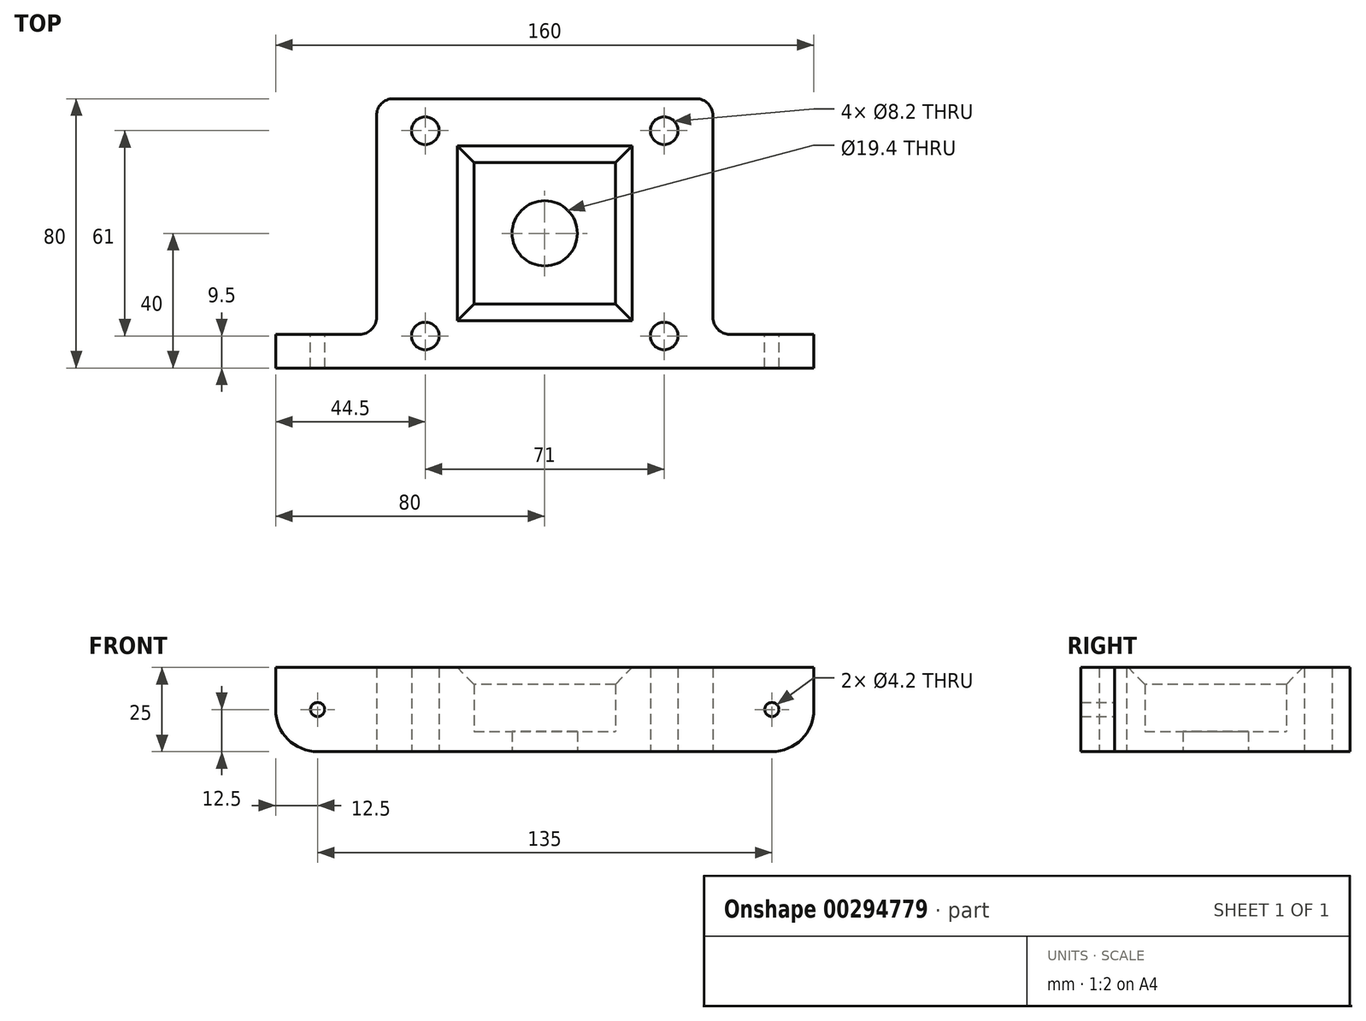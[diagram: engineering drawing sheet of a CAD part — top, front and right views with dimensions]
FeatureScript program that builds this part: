
annotation { "Feature Type Name" : "Feature", "Feature Type Description" : "" }
export const myFeature = defineFeature(function(context is Context, id is Id, definition is map)
    precondition{}
    {
        {
            var Q0;
            Q0=qCreatedBy(makeId("Top.planeOp"),FACE);
            var sketch = newSketch(context, id + "F0", { "sketchPlane" : qUnion([Q0])});
            skLineSegment(sketch, "E0.top", {"start": v(-50, -40) * mm, "end": v(50, -40) * mm});
            skPoint(sketch, "E0.middle", {"position": v(0, 0) * mm});
            skPoint(sketch, "E1.orphan", {"position": v(-50, 40) * mm});
            skPoint(sketch, "E2.orphan", {"position": v(50, 40) * mm});
            skPoint(sketch, "E0.left.start.orphan", {"position": v(-50, 21) * mm});
            skPoint(sketch, "E0.right.start.orphan", {"position": v(50, 21) * mm});
            skLineSegment(sketch, "E3", {"start": v(-50, 40) * mm, "end": v(-50, -40) * mm});
            skLineSegment(sketch, "E4", {"start": v(50, 40) * mm, "end": v(50, -40) * mm});
            skLineSegment(sketch, "E5", {"start": v(50, 40) * mm, "end": v(-50, 40) * mm});
            skLineSegment(sketch, "E6", {"start": v(50, 21) * mm, "end": v(21, 21) * mm, "construction": true});
            skLineSegment(sketch, "E7", {"start": v(-50, -40) * mm, "end": v(-21, -21) * mm, "construction": true});
            skLineSegment(sketch, "E8", {"start": v(-21, -21) * mm, "end": v(-50, -21) * mm, "construction": true});
            skLineSegment(sketch, "E9", {"start": v(-21, -21) * mm, "end": v(-21, -40) * mm, "construction": true});
            skLineSegment(sketch, "E10", {"start": v(-21, -40) * mm, "end": v(-50, -21) * mm, "construction": true});
            skLineSegment(sketch, "E11", {"start": v(-50, 21) * mm, "end": v(-21, 21) * mm, "construction": true});
            skLineSegment(sketch, "E12", {"start": v(21, -21) * mm, "end": v(21, -40) * mm, "construction": true});
            skLineSegment(sketch, "E13", {"start": v(21, -21) * mm, "end": v(50, -21) * mm, "construction": true});
            skLineSegment(sketch, "E14", {"start": v(50, -21) * mm, "end": v(21, -40) * mm, "construction": true});
            skLineSegment(sketch, "E15", {"start": v(50, -40) * mm, "end": v(21, -21) * mm, "construction": true});
            skCircle(sketch, "E16", {"center": v(-35.5, -30.5) * mm, "radius": 4.1 * mm});
            skCircle(sketch, "E17", {"center": v(35.5, -30.5) * mm, "radius": 4.1 * mm});
            skLineSegment(sketch, "E18", {"start": v(-21, 21) * mm, "end": v(-21, 40) * mm, "construction": true});
            skLineSegment(sketch, "E19", {"start": v(21, 21) * mm, "end": v(21, 40) * mm, "construction": true});
            skLineSegment(sketch, "E20", {"start": v(-21, 40) * mm, "end": v(-50, 21) * mm, "construction": true});
            skLineSegment(sketch, "E21", {"start": v(-50, 40) * mm, "end": v(-21, 21) * mm, "construction": true});
            skLineSegment(sketch, "E22", {"start": v(21, 40) * mm, "end": v(50, 21) * mm, "construction": true});
            skLineSegment(sketch, "E23", {"start": v(50, 40) * mm, "end": v(21, 21) * mm, "construction": true});
            skCircle(sketch, "E24", {"center": v(-35.5, 30.5) * mm, "radius": 4.1 * mm});
            skCircle(sketch, "E25", {"center": v(35.5, 30.5) * mm, "radius": 4.1 * mm});
            skCircle(sketch, "E26", {"center": v(0, 0) * mm, "radius": 9.7 * mm});
            skLineSegment(sketch, "E27.bottom", {"start": v(50, -40) * mm, "end": v(80, -40) * mm});
            skLineSegment(sketch, "E27.top", {"start": v(50, -30) * mm, "end": v(80, -30) * mm});
            skLineSegment(sketch, "E27.left", {"start": v(50, -40) * mm, "end": v(50, -30) * mm});
            skLineSegment(sketch, "E27.right", {"start": v(80, -40) * mm, "end": v(80, -30) * mm});
            skLineSegment(sketch, "E28.bottom", {"start": v(-50, -40) * mm, "end": v(-80, -40) * mm});
            skLineSegment(sketch, "E28.top", {"start": v(-50, -30) * mm, "end": v(-80, -30) * mm});
            skLineSegment(sketch, "E28.left", {"start": v(-50, -40) * mm, "end": v(-50, -30) * mm});
            skLineSegment(sketch, "E28.right", {"start": v(-80, -40) * mm, "end": v(-80, -30) * mm});
            skLineSegment(sketch, "E29", {"start": v(-21, 21) * mm, "end": v(21, 21) * mm});
            skLineSegment(sketch, "E30", {"start": v(21, 21) * mm, "end": v(21, -21) * mm});
            skLineSegment(sketch, "E31", {"start": v(21, -21) * mm, "end": v(-21, -21) * mm});
            skLineSegment(sketch, "E32", {"start": v(-21, -21) * mm, "end": v(-21, 21) * mm});
            skSolve(sketch);
        }
        {
            var Q0;
            Q0=makeQuery(id+"F0.imprint","IMPRINT",FACE,{"disambiguationData":[TD([[makeQuery(id+"F0.imprint","IMPRINT",EDGE,{"derivedFrom":sQuery(id+"F0.wireOp",EDGE,"E0.top")}),1.0]])]});
            var Q1;
            Q1=makeQuery(id+"F0.imprint","IMPRINT",FACE,{"disambiguationData":[TD([[makeQuery(id+"F0.imprint","IMPRINT",EDGE,{"derivedFrom":sQuery(id+"F0.wireOp",EDGE,"E28.bottom")}),-1.0]])]});
            var Q2;
            Q2=makeQuery(id+"F0.imprint","IMPRINT",FACE,{"disambiguationData":[TD([[makeQuery(id+"F0.imprint","IMPRINT",EDGE,{"derivedFrom":sQuery(id+"F0.wireOp",EDGE,"E27.bottom")}),1.0]])]});
            extrude(context, id + "F1", {"entities" : qUnion([Q0, Q1, Q2]), "depth" : 25 * mm});
        }
        {
            var Q0;
            Q0=makeQuery(id+"F0.imprint","IMPRINT",FACE,{"disambiguationData":[TD([[makeQuery(id+"F0.imprint","IMPRINT",EDGE,{"derivedFrom":sQuery(id+"F0.wireOp",EDGE,"E26")}),-1.0]])]});
            extrude(context, id + "F2", {"entities" : qUnion([Q0]), "operationType" : NewBodyOperationType.ADD, "depth" : 6 * mm});
        }
        {
            var Q0;
            Q0=makeQuery(id+"F1.opExtrude","CAP_EDGE",EDGE,{"disambiguationData":[OSD([sQuery(id+"F0.wireOp",EDGE,"E29")])],"isStart":false});
            var Q1;
            Q1=makeQuery(id+"F1.opExtrude","CAP_EDGE",EDGE,{"disambiguationData":[OSD([sQuery(id+"F0.wireOp",EDGE,"E32")])],"isStart":false});
            var Q2;
            Q2=makeQuery(id+"F1.opExtrude","CAP_EDGE",EDGE,{"disambiguationData":[OSD([sQuery(id+"F0.wireOp",EDGE,"E31")])],"isStart":false});
            var Q3;
            Q3=makeQuery(id+"F1.opExtrude","CAP_EDGE",EDGE,{"disambiguationData":[OSD([sQuery(id+"F0.wireOp",EDGE,"E30")])],"isStart":false});
            chamfer(context, id + "F3", {"entities" : qUnion([Q0, Q1, Q2, Q3]), "width" : 5 * mm, "tangentPropagation" : true});
        }
        {
            var Q0;
            Q0=makeQuery(id+"F1.opExtrude","SWEPT_EDGE",EDGE,{"disambiguationData":[OSD([sQuery(id+"F0.wireOp",EDGE,"E3"),sQuery(id+"F0.wireOp",EDGE,"E28.top"),sQuery(id+"F0.wireOp",EDGE,"E28.left")])]});
            var Q1;
            Q1=makeQuery(id+"F1.opExtrude","SWEPT_EDGE",EDGE,{"disambiguationData":[OSD([sQuery(id+"F0.wireOp",EDGE,"E3"),sQuery(id+"F0.wireOp",EDGE,"E5")])]});
            var Q2;
            Q2=makeQuery(id+"F1.opExtrude","SWEPT_EDGE",EDGE,{"disambiguationData":[OSD([sQuery(id+"F0.wireOp",EDGE,"E4"),sQuery(id+"F0.wireOp",EDGE,"E5")])]});
            var Q3;
            Q3=makeQuery(id+"F1.opExtrude","SWEPT_EDGE",EDGE,{"disambiguationData":[OSD([sQuery(id+"F0.wireOp",EDGE,"E4"),sQuery(id+"F0.wireOp",EDGE,"E27.top"),sQuery(id+"F0.wireOp",EDGE,"E27.left")])]});
            fillet(context, id + "F4", {"entities" : qUnion([Q0, Q1, Q2, Q3]), "radius" : 5 * mm, "tangentPropagation" : true, "allowEdgeOverflow" : false});
        }
        {
            var Q0;
            Q0=makeQuery(id+"F1.opExtrude","CAP_EDGE",EDGE,{"disambiguationData":[OSD([sQuery(id+"F0.wireOp",EDGE,"E27.right")])],"isStart":true});
            var Q1;
            Q1=makeQuery(id+"F1.opExtrude","CAP_EDGE",EDGE,{"disambiguationData":[OSD([sQuery(id+"F0.wireOp",EDGE,"E28.right")])],"isStart":true});
            fillet(context, id + "F5", {"entities" : qUnion([Q0, Q1]), "radius" : 12.5 * mm, "tangentPropagation" : true, "allowEdgeOverflow" : false});
        }
        {
            var Q0;
            Q0=makeQuery(id+"F1.opExtrude","SWEPT_FACE",FACE,{"disambiguationData":[OSD([sQuery(id+"F0.wireOp",EDGE,"E28.top")])]});
            var sketch = newSketch(context, id + "F6", { "sketchPlane" : qUnion([Q0])});
            skLineSegment(sketch, "E33", {"start": v(55, 25) * mm, "end": v(80, 0) * mm, "construction": true});
            skLineSegment(sketch, "E34", {"start": v(80, 25) * mm, "end": v(55, 0) * mm, "construction": true});
            skCircle(sketch, "E35", {"center": v(67.5, 12.5) * mm, "radius": 2.1 * mm});
            skSolve(sketch);
        }
        {
            var Q0;
            Q0=makeQuery(id+"F1.opExtrude","SWEPT_FACE",FACE,{"disambiguationData":[OSD([sQuery(id+"F0.wireOp",EDGE,"E27.top")])]});
            var sketch = newSketch(context, id + "F7", { "sketchPlane" : qUnion([Q0])});
            skLineSegment(sketch, "E36", {"start": v(-80, 25) * mm, "end": v(-55, 0) * mm, "construction": true});
            skLineSegment(sketch, "E37", {"start": v(-55, 25) * mm, "end": v(-80, 0) * mm, "construction": true});
            skCircle(sketch, "E38", {"center": v(-67.5, 12.5) * mm, "radius": 2.1 * mm});
            skSolve(sketch);
        }
        {
            var Q0;
            Q0=makeQuery(id+"F7.imprint","IMPRINT",FACE,{"disambiguationData":[TD([[makeQuery(id+"F7.imprint","IMPRINT",EDGE,{"derivedFrom":sQuery(id+"F7.wireOp",EDGE,"E38")}),1.0]])]});
            var Q1;
            Q1=makeQuery(id+"F6.imprint","IMPRINT",FACE,{"disambiguationData":[TD([[makeQuery(id+"F6.imprint","IMPRINT",EDGE,{"derivedFrom":sQuery(id+"F6.wireOp",EDGE,"E35")}),1.0]])]});
            extrude(context, id + "F8", {"entities" : qUnion([Q0, Q1]), "operationType" : NewBodyOperationType.REMOVE, "oppositeDirection" : true, "depth" : 25 * mm});
        }
    });
